# Revit family: Backwater_Valve_7150_JRSmith
name_source: partatom
category: Plumbing Fixtures
revit_build: Autodesk Revit MEP 2012 (Build: 20110309_2315(x64)
units: mm (PartAtom-declared; Revit-internal decimal feet)

## types (2) — shared parameters
04 CSI = 22 05 23
95 CSI = 15110
Action = Gate with Flapper
Assembly Code = D2030400
Caulk Connection = No
Default Elevation = 48"
Description = Duco cast iron body and cover with removable wheel handle, bronze gate and flapper valve
F = 5"
Manufacturer = Jay R. Smith Mfg. Co.
Material = Duco Yellow
Material Finish = Duco Yellow
Model = 7150
No-Hub Connection = No
OmniClass Code = 22-22 13 19 33
OmniClass Title = Backwater Valves
Product URL = http://www.jrsmith.com
SMARTBIM Object Version = 3
SMARTBIM URL = www.smartbim.com
Technical and Installation = http://www.jrsmith.com
URL = http://www.jrsmith.com
Warranty = 1 year material and workmanship

## per-type parameters (varying)
| type | A | B | C | D | E | G | Pipe Size | Radius | Radius 2 | Radius B | Weight (lb) |
| 7150-04 | 4" | 8" | 18" | 3 3/4" | 12" | 5 61/128" | 4" | 2" | 2 99/256" | 4" | 70.33 |
| 7150-06 | 6" | 10 1/2" | 20" | 5" | 14 1/2" | 7 61/128" | 6" | 3" | 3 99/256" | 5 1/4" | 118.69 |

## geometry (parser evidence)
native form markers: Blend x4, Sweep x5
no freeform markers — native parametric forms only
